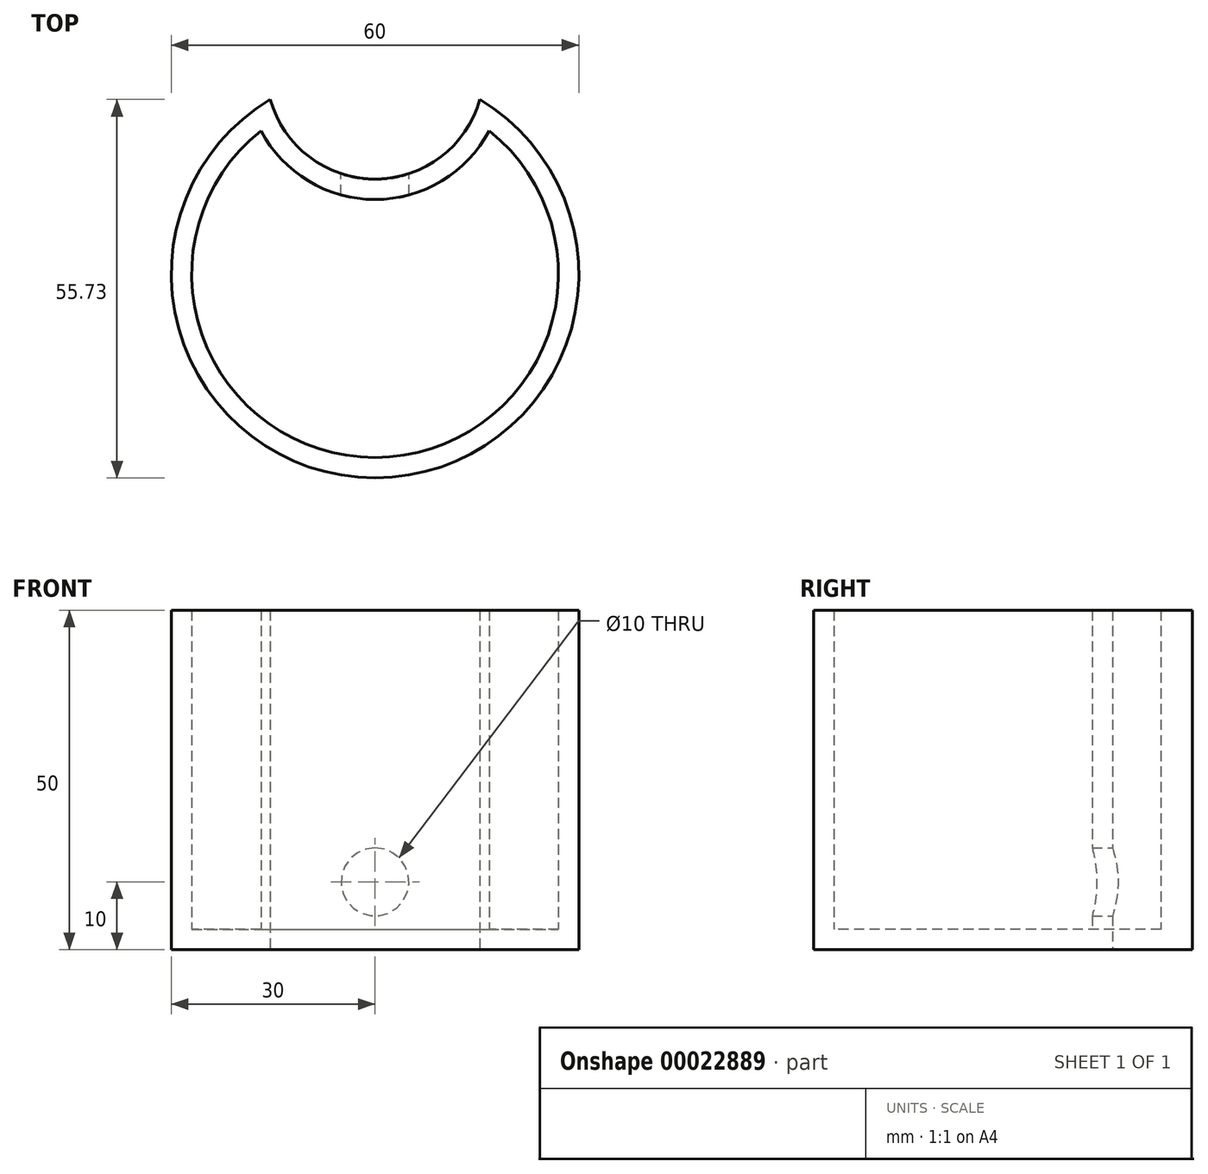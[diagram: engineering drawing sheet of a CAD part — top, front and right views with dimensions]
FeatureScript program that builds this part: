
annotation { "Feature Type Name" : "Feature", "Feature Type Description" : "" }
export const myFeature = defineFeature(function(context is Context, id is Id, definition is map)
    precondition{}
    {
        {
            var Q0;
            Q0=qCreatedBy(makeId("Top.planeOp"),FACE);
            var sketch = newSketch(context, id + "F0", { "sketchPlane" : qUnion([Q0])});
            skArc(sketch, "E0", {"start": v(-15.42, -4.27) * mm, "mid": v(0, -16) * mm, "end": v(15.42, -4.27) * mm});
            skArc(sketch, "E1", {"start": v(-15.42, -4.27) * mm, "mid": v(0, -60) * mm, "end": v(15.42, -4.27) * mm});
            skSolve(sketch);
        }
        {
            var Q0;
            Q0=makeQuery(id+"F0.imprint","IMPRINT",FACE,{"disambiguationData":[TD([[makeQuery(id+"F0.imprint","IMPRINT",EDGE,{"derivedFrom":sQuery(id+"F0.wireOp",EDGE,"E0")}),-1.0]])]});
            extrude(context, id + "F1", {"entities" : qUnion([Q0]), "depth" : 50 * mm});
        }
        {
            var Q0;
            Q0=makeQuery(id+"F1.opExtrude","CAP_FACE",FACE,{"disambiguationData":[OSD([sQuery(id+"F0.wireOp",EDGE,"E0"),sQuery(id+"F0.wireOp",EDGE,"E1")])],"isStart":false});
            shell(context, id + "F2", {"entities" : qUnion([Q0]), "thickness" : 3 * mm});
        }
        {
            var Q0;
            Q0=qCreatedBy(makeId("Front.planeOp"),FACE);
            var sketch = newSketch(context, id + "F3", { "sketchPlane" : qUnion([Q0])});
            skPoint(sketch, "E2", {"position": v(0, 10) * mm});
            skSolve(sketch);
        }
        {
            var Q0;
            Q0=sQuery(id+"F3.wireOp",VERTEX,"E2");
            var Q1;
            Q1=makeQuery(id+"F1.opExtrude","SWEPT_BODY",BODY,{"disambiguationData":[OSD([sQuery(id+"F0.wireOp",EDGE,"E0"),sQuery(id+"F0.wireOp",EDGE,"E1")])]});
            hole(context, id + "F4", {"style" : HoleStyle.SIMPLE, "holeDiameter" : 10 * mm, "endStyle" : HoleEndStyle.BLIND, "oppositeDirection" : true, "holeDepth" : 5 * mm, "locations" : qUnion([Q0]), "scope" : qUnion([Q1])});
        }
    });
